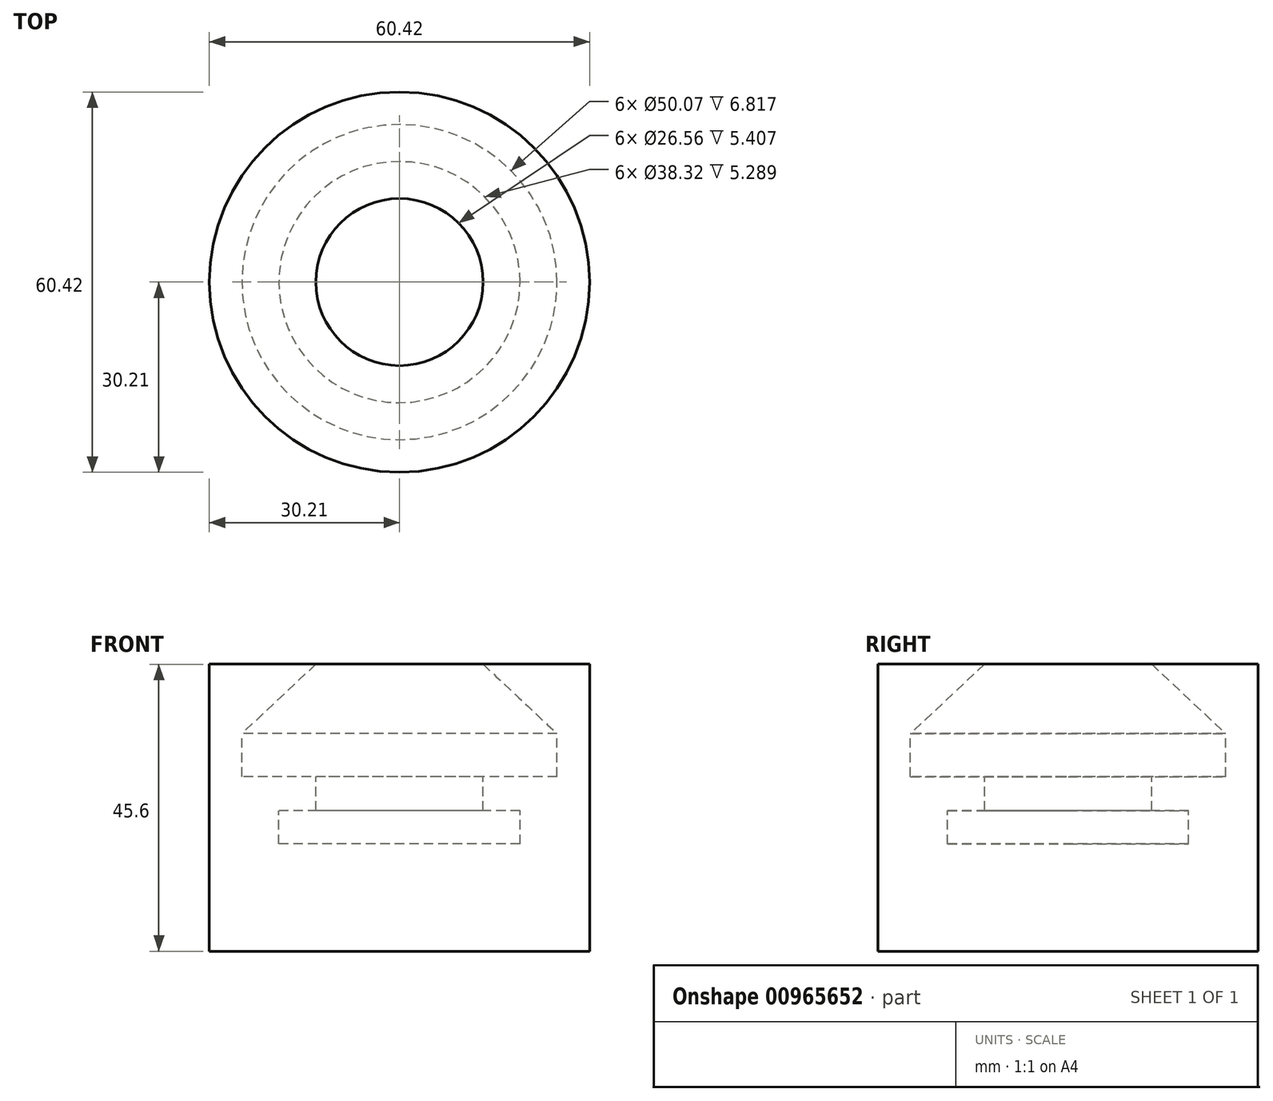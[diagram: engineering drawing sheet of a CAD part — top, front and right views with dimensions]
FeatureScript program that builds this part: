
annotation { "Feature Type Name" : "Feature", "Feature Type Description" : "" }
export const myFeature = defineFeature(function(context is Context, id is Id, definition is map)
    precondition{}
    {
        {
            var Q0;
            Q0=qCreatedBy(makeId("Front.planeOp"),FACE);
            var sketch = newSketch(context, id + "F0", { "sketchPlane" : qUnion([Q0])});
            skLineSegment(sketch, "E0", {"start": v(0, 0) * mm, "end": v(0, -17.04) * mm});
            skLineSegment(sketch, "E1", {"start": v(0, -17.04) * mm, "end": v(30.2, -17.04) * mm});
            skLineSegment(sketch, "E2", {"start": v(30.2, -17.04) * mm, "end": v(30.2, 28.56) * mm});
            skLineSegment(sketch, "E3", {"start": v(30.2, 28.56) * mm, "end": v(13.28, 28.56) * mm});
            skLineSegment(sketch, "E4", {"start": v(13.28, 28.56) * mm, "end": v(25.04, 17.51) * mm});
            skLineSegment(sketch, "E5", {"start": v(25.04, 17.51) * mm, "end": v(25.04, 10.7) * mm});
            skLineSegment(sketch, "E6", {"start": v(25.04, 10.7) * mm, "end": v(13.28, 10.7) * mm});
            skLineSegment(sketch, "E7", {"start": v(13.28, 10.7) * mm, "end": v(13.28, 5.29) * mm});
            skLineSegment(sketch, "E8", {"start": v(13.28, 5.29) * mm, "end": v(19.16, 5.29) * mm});
            skPoint(sketch, "E8.endSnap0", {"position": v(19.16, 10.7) * mm});
            skLineSegment(sketch, "E9", {"start": v(19.16, 5.29) * mm, "end": v(19.16, 0) * mm});
            skLineSegment(sketch, "E10", {"start": v(19.16, 0) * mm, "end": v(0, 0) * mm});
            skSolve(sketch);
        }
        {
            var Q0;
            Q0=makeQuery(id+"F0.imprint","IMPRINT",FACE,{"disambiguationData":[TD([[makeQuery(id+"F0.imprint","IMPRINT",EDGE,{"derivedFrom":sQuery(id+"F0.wireOp",EDGE,"E0")}),1.0]])]});
            var Q1;
            Q1=sQuery(id+"F0.wireOp",EDGE,"E0");
            revolve(context, id + "F1", {"surfaceOperationType" : NewSurfaceOperationType.NEW, "entities" : qUnion([Q0]), "axis" : qUnion([Q1]), "revolveType" : RevolveType.FULL});
        }
    });
